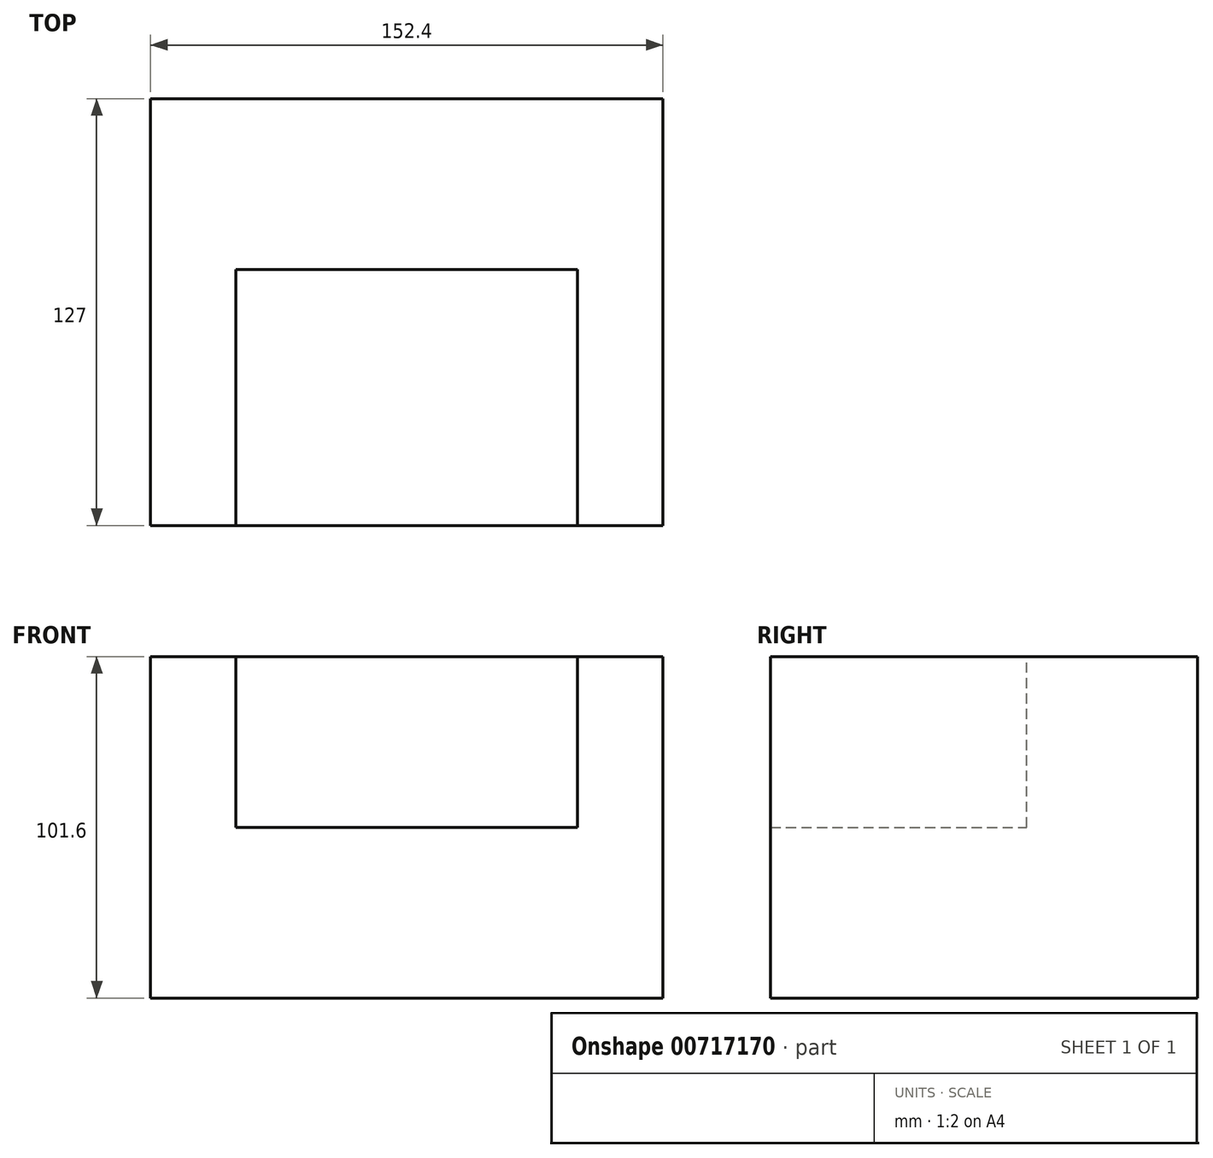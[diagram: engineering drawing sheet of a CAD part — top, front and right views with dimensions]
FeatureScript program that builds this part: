
annotation { "Feature Type Name" : "Feature", "Feature Type Description" : "" }
export const myFeature = defineFeature(function(context is Context, id is Id, definition is map)
    precondition{}
    {
        {
            var Q0;
            Q0=qCreatedBy(makeId("Front.planeOp"),FACE);
            var sketch = newSketch(context, id + "F0", { "sketchPlane" : qUnion([Q0])});
            skLineSegment(sketch, "E0", {"start": v(-127, -30.22) * mm, "end": v(25.4, -30.22) * mm});
            skLineSegment(sketch, "E1", {"start": v(25.4, -30.22) * mm, "end": v(25.4, 71.38) * mm});
            skLineSegment(sketch, "E2", {"start": v(25.4, 71.38) * mm, "end": v(0, 71.38) * mm});
            skLineSegment(sketch, "E3", {"start": v(0, 71.38) * mm, "end": v(0, 20.58) * mm});
            skLineSegment(sketch, "E4", {"start": v(0, 20.58) * mm, "end": v(-101.6, 20.58) * mm});
            skLineSegment(sketch, "E5", {"start": v(-101.6, 20.58) * mm, "end": v(-101.6, 71.38) * mm});
            skLineSegment(sketch, "E6", {"start": v(-101.6, 71.38) * mm, "end": v(-127, 71.38) * mm});
            skLineSegment(sketch, "E7", {"start": v(-127, 71.38) * mm, "end": v(-127, -30.22) * mm});
            skSolve(sketch);
        }
        {
            var Q0;
            Q0=makeQuery(id+"F0.imprint","IMPRINT",FACE,{"disambiguationData":[TD([[makeQuery(id+"F0.imprint","IMPRINT",EDGE,{"derivedFrom":sQuery(id+"F0.wireOp",EDGE,"E0")}),1.0]])]});
            extrude(context, id + "F1", {"entities" : qUnion([Q0]), "depth" : 127 * mm, "offsetDistance" : 25.4 * mm});
        }
        {
            var Q0;
            Q0=makeQuery(id+"F1.opExtrude","SWEPT_FACE",FACE,{"disambiguationData":[OSD([sQuery(id+"F0.wireOp",EDGE,"E5")])]});
            var sketch = newSketch(context, id + "F2", { "sketchPlane" : qUnion([Q0])});
            skLineSegment(sketch, "E8", {"start": v(-50.8, 71.38) * mm, "end": v(0, 71.38) * mm});
            skLineSegment(sketch, "E9", {"start": v(0, 71.38) * mm, "end": v(0, 20.58) * mm});
            skLineSegment(sketch, "E10", {"start": v(0, 20.58) * mm, "end": v(-50.8, 20.58) * mm});
            skLineSegment(sketch, "E11", {"start": v(-50.8, 20.58) * mm, "end": v(0, 20.58) * mm});
            skLineSegment(sketch, "E12", {"start": v(-50.8, 20.58) * mm, "end": v(-50.8, 71.38) * mm});
            skSolve(sketch);
        }
        {
            var Q0;
            Q0=makeQuery(id+"F2.imprint","IMPRINT",FACE,{"disambiguationData":[TD([[makeQuery(id+"F2.imprint","IMPRINT",EDGE,{"derivedFrom":sQuery(id+"F2.wireOp",EDGE,"E8")}),-1.0]])]});
            extrude(context, id + "F3", {"entities" : qUnion([Q0]), "operationType" : NewBodyOperationType.ADD, "depth" : 101.6 * mm, "offsetDistance" : 25.4 * mm});
        }
    });
